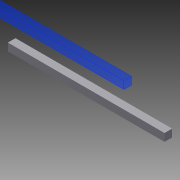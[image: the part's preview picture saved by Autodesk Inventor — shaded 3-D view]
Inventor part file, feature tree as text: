
AUTODESK INVENTOR PART (.ipt)
format: ipt  version: 2012 (Build 160160000, 160)  size: 94,208 bytes
history: native  units: in
note: dims shown in document units (in); Inventor stores cm internally (conversion verified against a paired STEP export)
features: reference x6, sketch x2, extrude x1, hole x1
ambient origin geometry x8: Origin, YZ Plane, XZ Plane, XY Plane, X Axis, Y Axis, Z Axis, Center Point
bodies: Solid1 (feature_tree)
feature tree (10):
  extrude  "Extrusion1"  Depth=7.7in
  hole  "Hole1"  [1 undecoded]
  sketch  "Sketch1"  dims[d0=0.375in d1=7.7in]
  sketch  "Sketch2"  dims[d2=0.375in d3=0.0in d4=0.1875in d5=0.1875in d6=0.1875in d7=0.1875in d8=0.1875in d9=0.1875in d10=0.1875in d11=0.1875in d12=0.177in d13=0.75in d14=0.332in d15=0.25in d16=0.5635in d17=1.0in d18=0.8108in]
  reference  "Reference1"
  reference  "Reference2"
  reference  "Reference3"
  reference  "Reference4"
  reference  "Reference5"
  reference  "Reference6"
note: 1 required parameter value undecoded (feature->parameter linkage not recoverable at this tier; creation-order binding heuristic only, values carry confidence <= 0.55)
